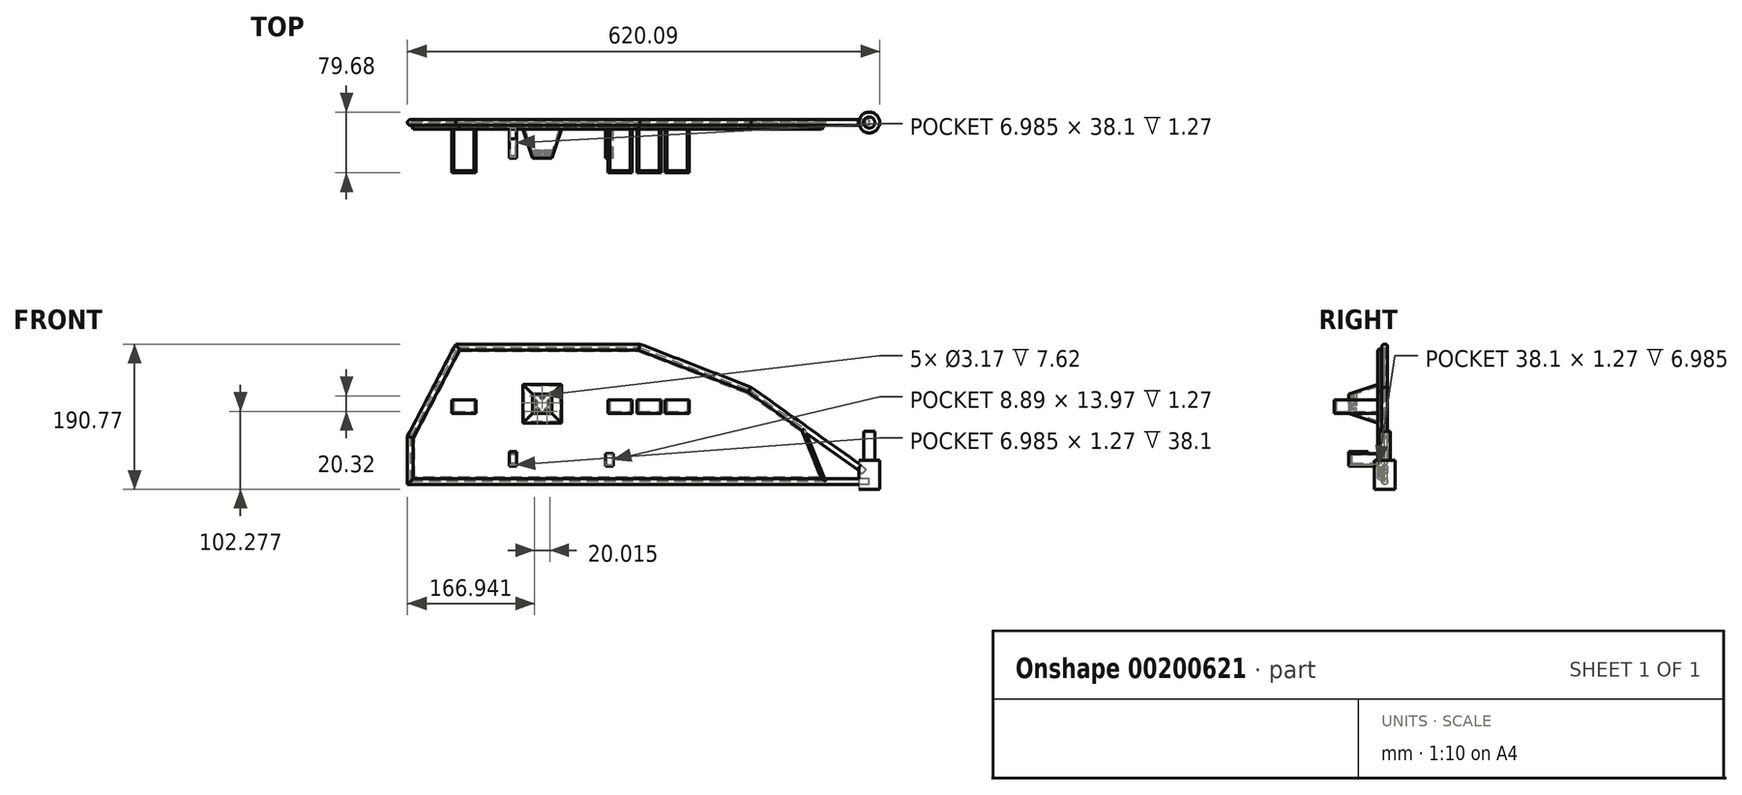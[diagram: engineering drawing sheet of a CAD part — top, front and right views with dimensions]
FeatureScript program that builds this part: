
annotation { "Feature Type Name" : "Feature", "Feature Type Description" : "" }
export const myFeature = defineFeature(function(context is Context, id is Id, definition is map)
    precondition{}
    {
        {
            var Q0;
            Q0=qCreatedBy(makeId("Top.planeOp"),FACE);
            var sketch = newSketch(context, id + "F0", { "sketchPlane" : qUnion([Q0])});
            skCircle(sketch, "E0", {"center": v(0, 0) * mm, "radius": 13.64 * mm});
            skSolve(sketch);
        }
        {
            var Q0;
            Q0 = qSketchRegion(id + "F0", true);
            extrude(context, id + "F1", {"entities" : qUnion([Q0]), "depth" : 38.1 * mm});
        }
        {
            var Q0;
            Q0=makeQuery(id+"F1.opExtrude","CAP_FACE",FACE,{"disambiguationData":[OSD([sQuery(id+"F0.wireOp",EDGE,"E0")])],"isStart":false});
            var sketch = newSketch(context, id + "F2", { "sketchPlane" : qUnion([Q0])});
            skCircle(sketch, "E1", {"center": v(0, 0) * mm, "radius": 7.35 * mm});
            skSolve(sketch);
        }
        {
            var Q0;
            Q0 = qSketchRegion(id + "F2", true);
            extrude(context, id + "F3", {"entities" : qUnion([Q0]), "operationType" : NewBodyOperationType.ADD, "depth" : 38.1 * mm});
        }
        {
            var Q0;
            Q0=qCreatedBy(makeId("Front.planeOp"),FACE);
            var sketch = newSketch(context, id + "F4", { "sketchPlane" : qUnion([Q0])});
            skLineSegment(sketch, "E2", {"start": v(-13.38, 28.84) * mm, "end": v(-157.18, 130.84) * mm});
            skLineSegment(sketch, "E3", {"start": v(-157.18, 130.84) * mm, "end": v(-301.75, 186.96) * mm});
            skLineSegment(sketch, "E4", {"start": v(-301.75, 186.96) * mm, "end": v(-541, 186.96) * mm});
            skLineSegment(sketch, "E5", {"start": v(-541, 186.96) * mm, "end": v(-602.64, 68.58) * mm});
            skLineSegment(sketch, "E6", {"start": v(-602.64, 68.58) * mm, "end": v(-602.64, 10.16) * mm});
            skLineSegment(sketch, "E7", {"start": v(-602.64, 10.16) * mm, "end": v(-13.38, 10.16) * mm});
            skPoint(sketch, "E8.end.orphan", {"position": v(-301.75, 70.79) * mm});
            skLineSegment(sketch, "E9", {"start": v(-13.38, 10.16) * mm, "end": v(0, 10.16) * mm});
            skLineSegment(sketch, "E10", {"start": v(-13.38, 28.84) * mm, "end": v(-6.69, 23.33) * mm});
            skPoint(sketch, "E10.endSnap0", {"position": v(-6.69, 10.16) * mm});
            skSolve(sketch);
        }
        {
            var Q0;
            Q0=qCreatedBy(makeId("Right.planeOp"),FACE);
            var sketch = newSketch(context, id + "F5", { "sketchPlane" : qUnion([Q0])});
            skCircle(sketch, "E11", {"center": v(0, 10.16) * mm, "radius": 3.81 * mm});
            skSolve(sketch);
        }
        {
            var Q0;
            Q0=makeQuery(id+"F5.imprint","IMPRINT",FACE,{"disambiguationData":[TD([[makeQuery(id+"F5.imprint","IMPRINT",EDGE,{"derivedFrom":sQuery(id+"F5.wireOp",EDGE,"E11")}),1.0]])]});
            var Q1;
            Q1=sQuery(id+"F4.wireOp",EDGE,"E7");
            var Q2;
            Q2=sQuery(id+"F4.wireOp",EDGE,"E9");
            var Q3;
            Q3=sQuery(id+"F4.wireOp",EDGE,"E6");
            var Q4;
            Q4=sQuery(id+"F4.wireOp",EDGE,"E5");
            var Q5;
            Q5=sQuery(id+"F4.wireOp",EDGE,"E4");
            var Q6;
            Q6=sQuery(id+"F4.wireOp",EDGE,"E3");
            var Q7;
            Q7=sQuery(id+"F4.wireOp",EDGE,"E2");
            var Q8;
            Q8=sQuery(id+"F4.wireOp",EDGE,"E10");
            sweep(context, id + "F6", {"profiles" : qUnion([Q0]), "path" : qUnion([Q1, Q2, Q3, Q4, Q5, Q6, Q7, Q8])});
        }
        {
            var Q0;
            Q0=qCreatedBy(makeId("Front.planeOp"),FACE);
            var sketch = newSketch(context, id + "F7", { "sketchPlane" : qUnion([Q0])});
            skLineSegment(sketch, "E12", {"start": v(-302.52, 186.67) * mm, "end": v(-540.3, 186.67) * mm});
            skLineSegment(sketch, "E13", {"start": v(-540.3, 186.67) * mm, "end": v(-602.41, 68.38) * mm});
            skLineSegment(sketch, "E14", {"start": v(-602.41, 68.38) * mm, "end": v(-602.41, 22.56) * mm});
            skLineSegment(sketch, "E15", {"start": v(-602.41, 22.56) * mm, "end": v(-602.41, 10.33) * mm});
            skLineSegment(sketch, "E16", {"start": v(-602.41, 10.33) * mm, "end": v(-57.1, 10.33) * mm});
            skLineSegment(sketch, "E17", {"start": v(-57.1, 10.33) * mm, "end": v(-85.52, 80.07) * mm});
            skLineSegment(sketch, "E18", {"start": v(-85.52, 80.07) * mm, "end": v(-157.4, 130.63) * mm});
            skLineSegment(sketch, "E19", {"start": v(-157.4, 130.63) * mm, "end": v(-302.52, 186.67) * mm});
            skSolve(sketch);
        }
        {
            var Q0;
            Q0 = qSketchRegion(id + "F7", true);
            extrude(context, id + "F8", {"entities" : qUnion([Q0]), "depth" : 8.9 * mm, "hasDraft" : true, "draftAngle" : 22 * degree, "draftPullDirection" : true});
        }
        {
            var Q0;
            Q0=makeQuery(id+"F8.opExtrude","CAP_FACE",FACE,{"disambiguationData":[OSD([sQuery(id+"F7.wireOp",EDGE,"E12"),sQuery(id+"F7.wireOp",EDGE,"E13"),sQuery(id+"F7.wireOp",EDGE,"E14"),sQuery(id+"F7.wireOp",EDGE,"E15"),sQuery(id+"F7.wireOp",EDGE,"E16"),sQuery(id+"F7.wireOp",EDGE,"E17"),sQuery(id+"F7.wireOp",EDGE,"E18"),sQuery(id+"F7.wireOp",EDGE,"E19")])],"isStart":false});
            var sketch = newSketch(context, id + "F9", { "sketchPlane" : qUnion([Q0])});
            skLineSegment(sketch, "E20.bottom", {"start": v(-404.1, 87.04) * mm, "end": v(-454.9, 87.04) * mm});
            skLineSegment(sketch, "E20.top", {"start": v(-404.1, 137.84) * mm, "end": v(-454.9, 137.84) * mm});
            skLineSegment(sketch, "E20.left", {"start": v(-404.1, 87.04) * mm, "end": v(-404.1, 137.84) * mm});
            skLineSegment(sketch, "E20.right", {"start": v(-454.9, 87.04) * mm, "end": v(-454.9, 137.84) * mm});
            skSolve(sketch);
        }
        {
            var Q0;
            Q0=makeQuery(id+"F9.imprint","IMPRINT",FACE,{"disambiguationData":[TD([[makeQuery(id+"F9.imprint","IMPRINT",EDGE,{"derivedFrom":sQuery(id+"F9.wireOp",EDGE,"E20.bottom")}),1.0]])]});
            cPlane(context, id + "F10", {"entities" : qUnion([Q0]), "cplaneType" : CPlaneType.OFFSET, "offset" : 38.1 * mm, "width" : 152.4 * mm, "height" : 152.4 * mm});
        }
        {
            var Q0;
            Q0=qCreatedBy(id+"F10.planeOp",FACE);
            var sketch = newSketch(context, id + "F11", { "sketchPlane" : qUnion([Q0])});
            skLineSegment(sketch, "E21.bottom", {"start": v(-442.2, 125.14) * mm, "end": v(-416.8, 125.14) * mm});
            skLineSegment(sketch, "E21.top", {"start": v(-442.2, 99.74) * mm, "end": v(-416.8, 99.74) * mm});
            skLineSegment(sketch, "E21.left", {"start": v(-442.2, 125.14) * mm, "end": v(-442.2, 99.74) * mm});
            skLineSegment(sketch, "E21.right", {"start": v(-416.8, 125.14) * mm, "end": v(-416.8, 99.74) * mm});
            skSolve(sketch);
        }
        {
            var Q1;
            Q1=makeQuery(id+"F9.imprint","IMPRINT",FACE,{"disambiguationData":[TD([[makeQuery(id+"F9.imprint","IMPRINT",EDGE,{"derivedFrom":sQuery(id+"F9.wireOp",EDGE,"E20.bottom")}),-1.0]])]});
            var Q2;
            Q2=makeQuery(id+"F11.imprint","IMPRINT",FACE,{"disambiguationData":[TD([[makeQuery(id+"F11.imprint","IMPRINT",EDGE,{"derivedFrom":sQuery(id+"F11.wireOp",EDGE,"E21.bottom")}),-1.0]])]});
            loft(context, id + "F12", {"operationType" : NewBodyOperationType.ADD, "sheetProfilesArray" : [{ "sheetProfileEntities" : qUnion([Q1]) }, { "sheetProfileEntities" : qUnion([Q2]) }]});
        }
        {
            var Q0;
            Q0=makeQuery(id+"F12.opLoft","CAP_FACE",FACE,{"disambiguationData":[OSD([makeQuery(id+"F11.imprint","IMPRINT",FACE,{"disambiguationData":[TD([[makeQuery(id+"F11.imprint","IMPRINT",EDGE,{"derivedFrom":sQuery(id+"F11.wireOp",EDGE,"E21.bottom")}),-1.0]])]})])],"isStart":true});
            var sketch = newSketch(context, id + "F13", { "sketchPlane" : qUnion([Q0])});
            skCircle(sketch, "E22", {"center": v(-429.5, 122.6) * mm, "radius": 1.59 * mm});
            skPoint(sketch, "E22.centerSnap0", {"position": v(-429.5, 125.14) * mm});
            skCircle(sketch, "E23", {"center": v(-419.5, 113.9) * mm, "radius": 1.59 * mm});
            skCircle(sketch, "E24", {"center": v(-439.5, 113.9) * mm, "radius": 1.59 * mm});
            skCircle(sketch, "E25", {"center": v(-423.3, 102.28) * mm, "radius": 1.59 * mm});
            skCircle(sketch, "E26", {"center": v(-435.7, 102.28) * mm, "radius": 1.59 * mm});
            skSolve(sketch);
        }
        {
            var Q0;
            Q0 = qSketchRegion(id + "F13", true);
            extrude(context, id + "F14", {"entities" : qUnion([Q0]), "operationType" : NewBodyOperationType.REMOVE, "oppositeDirection" : true, "depth" : 7.62 * mm});
        }
        {
            var Q0;
            Q0=makeQuery(id+"F8.opExtrude","CAP_FACE",FACE,{"disambiguationData":[OSD([sQuery(id+"F7.wireOp",EDGE,"E12"),sQuery(id+"F7.wireOp",EDGE,"E13"),sQuery(id+"F7.wireOp",EDGE,"E14"),sQuery(id+"F7.wireOp",EDGE,"E15"),sQuery(id+"F7.wireOp",EDGE,"E16"),sQuery(id+"F7.wireOp",EDGE,"E17"),sQuery(id+"F7.wireOp",EDGE,"E18"),sQuery(id+"F7.wireOp",EDGE,"E19")])],"isStart":false});
            var sketch = newSketch(context, id + "F15", { "sketchPlane" : qUnion([Q0])});
            skLineSegment(sketch, "E27.bottom", {"start": v(-548.25, 117.5) * mm, "end": v(-516.5, 117.5) * mm});
            skLineSegment(sketch, "E27.top", {"start": v(-548.25, 99.72) * mm, "end": v(-516.5, 99.72) * mm});
            skLineSegment(sketch, "E27.left", {"start": v(-548.25, 117.5) * mm, "end": v(-548.25, 99.72) * mm});
            skLineSegment(sketch, "E27.right", {"start": v(-516.5, 117.5) * mm, "end": v(-516.5, 99.72) * mm});
            skLineSegment(sketch, "E28.bottom", {"start": v(-342.9, 117.5) * mm, "end": v(-311.15, 117.5) * mm});
            skLineSegment(sketch, "E28.top", {"start": v(-342.9, 99.72) * mm, "end": v(-311.15, 99.72) * mm});
            skLineSegment(sketch, "E28.left", {"start": v(-342.9, 117.5) * mm, "end": v(-342.9, 99.72) * mm});
            skLineSegment(sketch, "E28.right", {"start": v(-311.15, 117.5) * mm, "end": v(-311.15, 99.72) * mm});
            skSolve(sketch);
        }
        {
            var Q0;
            Q0 = qSketchRegion(id + "F15", true);
            extrude(context, id + "F16", {"entities" : qUnion([Q0]), "operationType" : NewBodyOperationType.ADD, "depth" : 57.15 * mm});
        }
        {
            var Q0;
            Q0=makeQuery(id+"F8.opExtrude","CAP_FACE",FACE,{"disambiguationData":[OSD([sQuery(id+"F7.wireOp",EDGE,"E12"),sQuery(id+"F7.wireOp",EDGE,"E13"),sQuery(id+"F7.wireOp",EDGE,"E14"),sQuery(id+"F7.wireOp",EDGE,"E15"),sQuery(id+"F7.wireOp",EDGE,"E16"),sQuery(id+"F7.wireOp",EDGE,"E17"),sQuery(id+"F7.wireOp",EDGE,"E18"),sQuery(id+"F7.wireOp",EDGE,"E19")])],"isStart":false});
            var sketch = newSketch(context, id + "F17", { "sketchPlane" : qUnion([Q0])});
            skLineSegment(sketch, "E29.bottom", {"start": v(-304.8, 117.5) * mm, "end": v(-273.05, 117.5) * mm});
            skLineSegment(sketch, "E29.top", {"start": v(-304.8, 99.72) * mm, "end": v(-273.05, 99.72) * mm});
            skLineSegment(sketch, "E29.left", {"start": v(-304.8, 117.5) * mm, "end": v(-304.8, 99.72) * mm});
            skLineSegment(sketch, "E29.right", {"start": v(-273.05, 117.5) * mm, "end": v(-273.05, 99.72) * mm});
            skLineSegment(sketch, "E30.bottom", {"start": v(-267.97, 117.5) * mm, "end": v(-236.22, 117.5) * mm});
            skLineSegment(sketch, "E30.top", {"start": v(-267.97, 99.72) * mm, "end": v(-236.22, 99.72) * mm});
            skLineSegment(sketch, "E30.left", {"start": v(-267.97, 117.5) * mm, "end": v(-267.97, 99.72) * mm});
            skLineSegment(sketch, "E30.right", {"start": v(-236.22, 117.5) * mm, "end": v(-236.22, 99.72) * mm});
            skSolve(sketch);
        }
        {
            var Q0;
            Q0 = qSketchRegion(id + "F17", true);
            extrude(context, id + "F18", {"entities" : qUnion([Q0]), "operationType" : NewBodyOperationType.ADD, "depth" : 57.15 * mm});
        }
        {
            var Q0;
            Q0=makeQuery(id+"F16.opExtrude","SWEPT_FACE",FACE,{"disambiguationData":[OSD([sQuery(id+"F15.wireOp",EDGE,"E27.bottom")])]});
            var Q1;
            Q1=makeQuery(id+"F16.opExtrude","SWEPT_FACE",FACE,{"disambiguationData":[OSD([sQuery(id+"F15.wireOp",EDGE,"E28.bottom")])]});
            var Q2;
            Q2=makeQuery(id+"F18.opExtrude","SWEPT_FACE",FACE,{"disambiguationData":[OSD([sQuery(id+"F17.wireOp",EDGE,"E29.bottom")])]});
            var Q3;
            Q3=makeQuery(id+"F18.opExtrude","SWEPT_FACE",FACE,{"disambiguationData":[OSD([sQuery(id+"F17.wireOp",EDGE,"E30.bottom")])]});
            shell(context, id + "F19", {"entities" : qUnion([Q0, Q1, Q2, Q3]), "thickness" : 2.54 * mm});
        }
        {
            var Q0;
            Q0=makeQuery(id+"F8.opExtrude","CAP_FACE",FACE,{"disambiguationData":[OSD([sQuery(id+"F7.wireOp",EDGE,"E12"),sQuery(id+"F7.wireOp",EDGE,"E13"),sQuery(id+"F7.wireOp",EDGE,"E14"),sQuery(id+"F7.wireOp",EDGE,"E15"),sQuery(id+"F7.wireOp",EDGE,"E16"),sQuery(id+"F7.wireOp",EDGE,"E17"),sQuery(id+"F7.wireOp",EDGE,"E18"),sQuery(id+"F7.wireOp",EDGE,"E19")])],"isStart":false});
            var sketch = newSketch(context, id + "F20", { "sketchPlane" : qUnion([Q0])});
            skLineSegment(sketch, "E31.bottom", {"start": v(-336.24, 47.02) * mm, "end": v(-346.4, 47.02) * mm});
            skLineSegment(sketch, "E31.top", {"start": v(-336.24, 30.5) * mm, "end": v(-346.4, 30.5) * mm});
            skLineSegment(sketch, "E31.left", {"start": v(-336.24, 47.02) * mm, "end": v(-336.24, 30.5) * mm});
            skLineSegment(sketch, "E31.right", {"start": v(-346.4, 47.02) * mm, "end": v(-346.4, 30.5) * mm});
            skLineSegment(sketch, "E32.bottom", {"start": v(-463.03, 30.5) * mm, "end": v(-472.55, 30.5) * mm});
            skLineSegment(sketch, "E32.top", {"start": v(-463.03, 34.32) * mm, "end": v(-472.55, 34.32) * mm});
            skLineSegment(sketch, "E32.left", {"start": v(-463.03, 30.5) * mm, "end": v(-463.03, 34.32) * mm});
            skLineSegment(sketch, "E32.right", {"start": v(-472.55, 30.5) * mm, "end": v(-472.55, 34.32) * mm});
            skSolve(sketch);
        }
        {
            var Q0;
            Q0 = qSketchRegion(id + "F20", true);
            extrude(context, id + "F21", {"entities" : qUnion([Q0]), "operationType" : NewBodyOperationType.ADD, "depth" : 38.1 * mm});
        }
        {
            var Q0;
            Q0=makeQuery(id+"F21.opExtrude","SWEPT_FACE",FACE,{"disambiguationData":[OSD([sQuery(id+"F20.wireOp",EDGE,"E31.right")])]});
            shell(context, id + "F22", {"entities" : qUnion([Q0]), "thickness" : 1.27 * mm});
        }
        {
            var Q0;
            Q0=makeQuery(id+"F21.opExtrude","SWEPT_FACE",FACE,{"disambiguationData":[OSD([sQuery(id+"F20.wireOp",EDGE,"E32.top")])]});
            var sketch = newSketch(context, id + "F23", { "sketchPlane" : qUnion([Q0])});
            skLineSegment(sketch, "E33.bottom", {"start": v(-472.55, -47) * mm, "end": v(-463.03, -47) * mm});
            skLineSegment(sketch, "E33.top", {"start": v(-472.55, -43.18) * mm, "end": v(-463.03, -43.18) * mm});
            skLineSegment(sketch, "E33.left", {"start": v(-472.55, -47) * mm, "end": v(-472.55, -43.18) * mm});
            skLineSegment(sketch, "E33.right", {"start": v(-463.03, -47) * mm, "end": v(-463.03, -43.18) * mm});
            skSolve(sketch);
        }
        {
            var Q0;
            Q0 = qSketchRegion(id + "F23", true);
            extrude(context, id + "F24", {"entities" : qUnion([Q0]), "operationType" : NewBodyOperationType.ADD, "depth" : 15.24 * mm});
        }
        {
            var Q0;
            Q0=makeQuery(id+"F24.opExtrude","SWEPT_FACE",FACE,{"disambiguationData":[OSD([sQuery(id+"F23.wireOp",EDGE,"E33.top")])]});
            var sketch = newSketch(context, id + "F25", { "sketchPlane" : qUnion([Q0])});
            skLineSegment(sketch, "E34.bottom", {"start": v(463.03, 49.56) * mm, "end": v(472.55, 49.56) * mm});
            skLineSegment(sketch, "E34.top", {"start": v(463.03, 45.75) * mm, "end": v(472.55, 45.75) * mm});
            skLineSegment(sketch, "E34.left", {"start": v(463.03, 49.56) * mm, "end": v(463.03, 45.75) * mm});
            skLineSegment(sketch, "E34.right", {"start": v(472.55, 49.56) * mm, "end": v(472.55, 45.75) * mm});
            skSolve(sketch);
        }
        {
            var Q0;
            Q0 = qSketchRegion(id + "F25", true);
            extrude(context, id + "F26", {"entities" : qUnion([Q0]), "operationType" : NewBodyOperationType.ADD, "depth" : 21.59 * mm});
        }
    });
